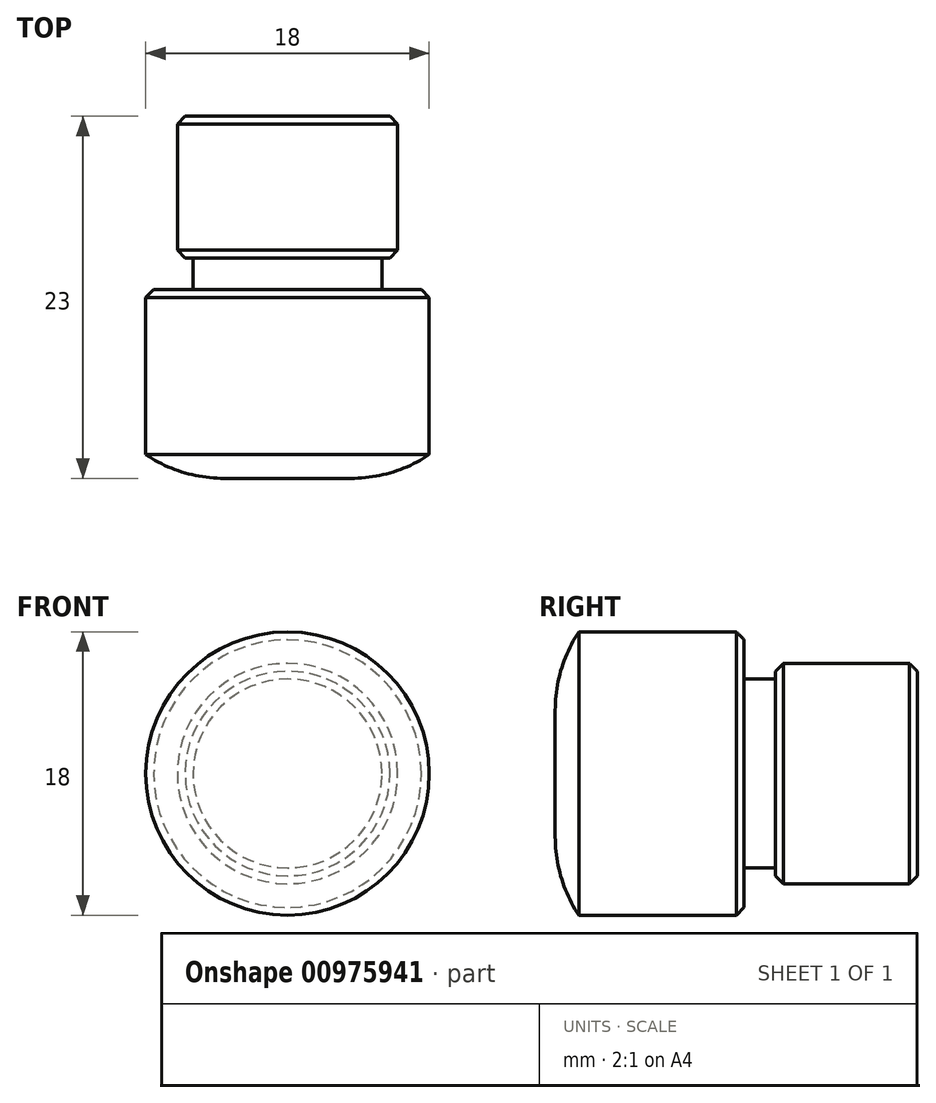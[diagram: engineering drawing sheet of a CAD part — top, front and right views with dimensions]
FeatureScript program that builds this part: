
annotation { "Feature Type Name" : "Feature", "Feature Type Description" : "" }
export const myFeature = defineFeature(function(context is Context, id is Id, definition is map)
    precondition{}
    {
        {
            var Q0;
            Q0=qCreatedBy(makeId("Front.planeOp"),FACE);
            var sketch = newSketch(context, id + "F0", { "sketchPlane" : qUnion([Q0])});
            skCircle(sketch, "E0", {"center": v(0, 0) * mm, "radius": 9 * mm});
            skSolve(sketch);
        }
        {
            var Q0;
            Q0=makeQuery(id+"F0.imprint","IMPRINT",FACE,{"disambiguationData":[TD([[makeQuery(id+"F0.imprint","IMPRINT",EDGE,{"derivedFrom":sQuery(id+"F0.wireOp",EDGE,"E0")}),1.0]])]});
            extrude(context, id + "F1", {"entities" : qUnion([Q0]), "depth" : 1.5 * mm, "offsetDistance" : 25 * mm});
        }
        {
            var Q0;
            Q0=makeQuery(id+"F1.opExtrude","CAP_EDGE",EDGE,{"disambiguationData":[OSD([sQuery(id+"F0.wireOp",EDGE,"E0")])],"isStart":false});
            fillet(context, id + "F2", {"entities" : qUnion([Q0]), "radius" : 9 * mm, "tangentPropagation" : true, "allowEdgeOverflow" : false});
        }
        {
            var Q0;
            Q0=makeQuery(id+"F1.opExtrude","CAP_FACE",FACE,{"disambiguationData":[OSD([sQuery(id+"F0.wireOp",EDGE,"E0")])],"isStart":true});
            var sketch = newSketch(context, id + "F3", { "sketchPlane" : qUnion([Q0])});
            skCircle(sketch, "E1", {"center": v(0, 0) * mm, "radius": 9 * mm});
            skSolve(sketch);
        }
        {
            var Q0;
            Q0=makeQuery(id+"F3.imprint","IMPRINT",FACE,{"disambiguationData":[TD([[makeQuery(id+"F3.imprint","IMPRINT",EDGE,{"derivedFrom":sQuery(id+"F3.wireOp",EDGE,"E1")}),-1.0]])]});
            extrude(context, id + "F4", {"entities" : qUnion([Q0]), "operationType" : NewBodyOperationType.ADD, "depth" : 10.5 * mm, "offsetDistance" : 25 * mm});
        }
        {
            var Q0;
            Q0=makeQuery(id+"F4.opExtrude","CAP_FACE",FACE,{"disambiguationData":[OSD([sQuery(id+"F3.wireOp",EDGE,"E1")])],"isStart":false});
            var sketch = newSketch(context, id + "F5", { "sketchPlane" : qUnion([Q0])});
            skCircle(sketch, "E2", {"center": v(0, 0) * mm, "radius": 6 * mm});
            skSolve(sketch);
        }
        {
            var Q0;
            Q0=makeQuery(id+"F5.imprint","IMPRINT",FACE,{"disambiguationData":[TD([[makeQuery(id+"F5.imprint","IMPRINT",EDGE,{"derivedFrom":sQuery(id+"F5.wireOp",EDGE,"E2")}),1.0]])]});
            extrude(context, id + "F6", {"entities" : qUnion([Q0]), "operationType" : NewBodyOperationType.ADD, "depth" : 2 * mm, "offsetDistance" : 25 * mm});
        }
        {
            var Q0;
            Q0=makeQuery(id+"F6.opExtrude","CAP_FACE",FACE,{"disambiguationData":[OSD([sQuery(id+"F5.wireOp",EDGE,"E2")])],"isStart":false});
            var sketch = newSketch(context, id + "F7", { "sketchPlane" : qUnion([Q0])});
            skCircle(sketch, "E3", {"center": v(0, 0) * mm, "radius": 7 * mm});
            skSolve(sketch);
        }
        {
            var Q0;
            Q0 = qSketchRegion(id + "F7", true);
            extrude(context, id + "F8", {"entities" : qUnion([Q0]), "operationType" : NewBodyOperationType.ADD, "depth" : 9 * mm, "offsetDistance" : 25 * mm});
        }
        {
            var Q0;
            Q0=makeQuery(id+"F6.opExtrude","CAP_EDGE",EDGE,{"disambiguationData":[OSD([sQuery(id+"F5.wireOp",EDGE,"E2")])],"isStart":false});
            var Q1;
            Q1=makeQuery(id+"F6.opExtrude","CAP_EDGE",EDGE,{"disambiguationData":[OSD([sQuery(id+"F5.wireOp",EDGE,"E2")])],"isStart":true});
            var Q2;
            Q2=makeQuery(id+"F4.opExtrude","CAP_EDGE",EDGE,{"disambiguationData":[OSD([sQuery(id+"F3.wireOp",EDGE,"E1")])],"isStart":false});
            var Q3;
            Q3=makeQuery(id+"F8.opExtrude","CAP_EDGE",EDGE,{"disambiguationData":[OSD([sQuery(id+"F7.wireOp",EDGE,"E3")])],"isStart":true});
            var Q4;
            Q4=makeQuery(id+"F8.opExtrude","CAP_EDGE",EDGE,{"disambiguationData":[OSD([sQuery(id+"F7.wireOp",EDGE,"E3")])],"isStart":false});
            chamfer(context, id + "F9", {"entities" : qUnion([Q0, Q1, Q2, Q3, Q4]), "width" : 0.5 * mm, "tangentPropagation" : true});
        }
    });
